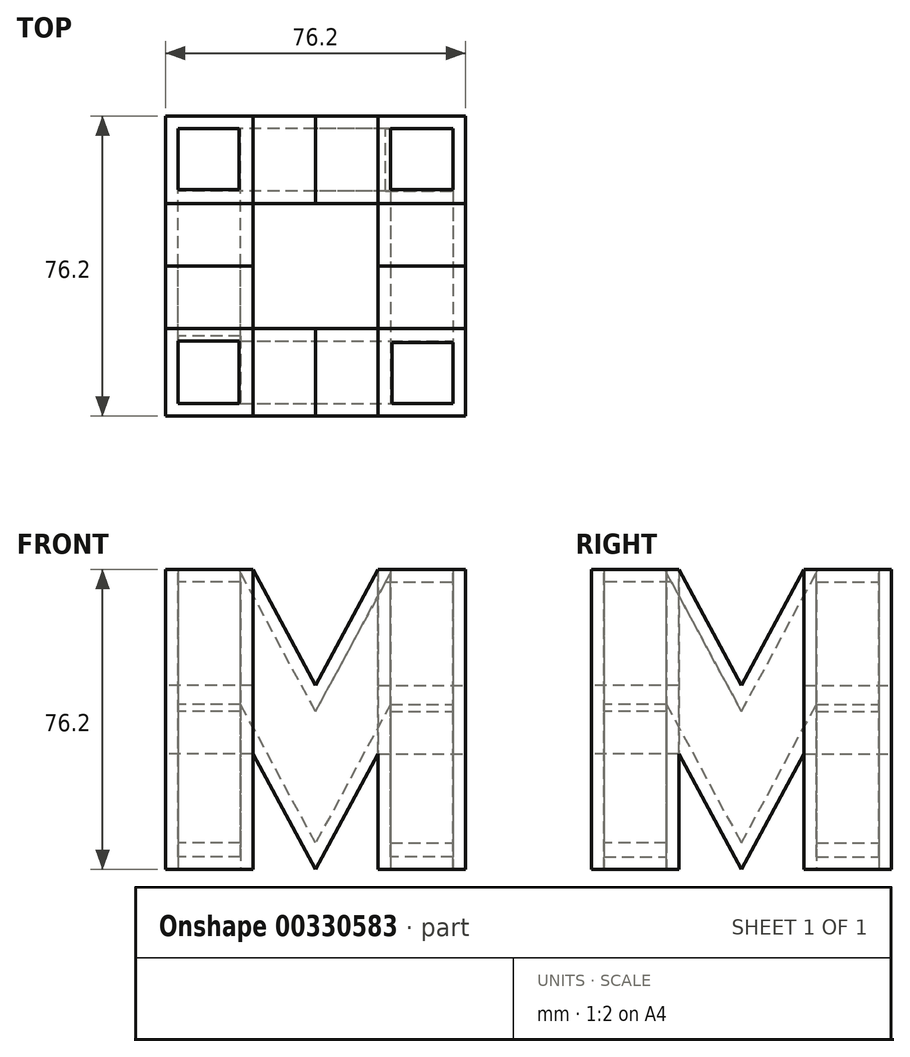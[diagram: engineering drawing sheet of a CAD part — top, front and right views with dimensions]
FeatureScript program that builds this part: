
annotation { "Feature Type Name" : "Feature", "Feature Type Description" : "" }
export const myFeature = defineFeature(function(context is Context, id is Id, definition is map)
    precondition{}
    {
        {
            var Q0;
            Q0=qCreatedBy(makeId("Front.planeOp"),FACE);
            var sketch = newSketch(context, id + "F0", { "sketchPlane" : qUnion([Q0])});
            skLineSegment(sketch, "E0.bottom", {"start": v(38.1, -38.1) * mm, "end": v(-38.1, -38.1) * mm, "construction": true});
            skLineSegment(sketch, "E0.top", {"start": v(38.1, 38.1) * mm, "end": v(-38.1, 38.1) * mm, "construction": true});
            skLineSegment(sketch, "E0.left", {"start": v(38.1, -38.1) * mm, "end": v(38.1, 38.1) * mm, "construction": true});
            skLineSegment(sketch, "E0.right", {"start": v(-38.1, -38.1) * mm, "end": v(-38.1, 38.1) * mm, "construction": true});
            skPoint(sketch, "E0.middle", {"position": v(0, 0) * mm});
            skLineSegment(sketch, "E1", {"start": v(-38.1, 38.1) * mm, "end": v(-38.1, -38.1) * mm});
            skLineSegment(sketch, "E2", {"start": v(-15.87, -38.1) * mm, "end": v(-15.87, -8.69) * mm});
            skLineSegment(sketch, "E3", {"start": v(15.88, -38.1) * mm, "end": v(38.1, -38.1) * mm});
            skLineSegment(sketch, "E4", {"start": v(38.1, 38.1) * mm, "end": v(15.88, 38.1) * mm});
            skLineSegment(sketch, "E5", {"start": v(-15.88, 38.1) * mm, "end": v(-38.1, 38.1) * mm});
            skLineSegment(sketch, "E6", {"start": v(38.1, 38.1) * mm, "end": v(38.1, -38.1) * mm});
            skLineSegment(sketch, "E7", {"start": v(-38.1, -38.1) * mm, "end": v(-15.87, -38.1) * mm});
            skLineSegment(sketch, "E8", {"start": v(-15.87, -8.69) * mm, "end": v(0, -38.1) * mm});
            skLineSegment(sketch, "E9", {"start": v(0, -38.1) * mm, "end": v(15.88, -8.69) * mm});
            skLineSegment(sketch, "E10", {"start": v(15.88, -8.69) * mm, "end": v(15.88, -38.1) * mm});
            skLineSegment(sketch, "E11", {"start": v(-15.88, 38.1) * mm, "end": v(0, 8.69) * mm});
            skLineSegment(sketch, "E12", {"start": v(0, 8.69) * mm, "end": v(15.88, 38.1) * mm});
            skLineSegment(sketch, "E13", {"start": v(15.87, -8.69) * mm, "end": v(-3.68, 1.87) * mm, "construction": true});
            skSolve(sketch);
        }
        {
            var Q0;
            Q0=makeQuery(id+"F0.imprint","IMPRINT",FACE,{"disambiguationData":[TD([[makeQuery(id+"F0.imprint","IMPRINT",EDGE,{"derivedFrom":sQuery(id+"F0.wireOp",EDGE,"E1")}),1.0]])]});
            extrude(context, id + "F1", {"entities" : qUnion([Q0]), "oppositeDirection" : true, "depth" : 22.22 * mm});
        }
        {
            var Q0;
            Q0=qCreatedBy(makeId("Top.planeOp"),FACE);
            var sketch = newSketch(context, id + "F2", { "sketchPlane" : qUnion([Q0])});
            skCircle(sketch, "E14", {"center": v(0, 38.1) * mm, "radius": 38.1 * mm, "construction": true});
            skLineSegment(sketch, "E15", {"start": v(38.1, 0) * mm, "end": v(0, 38.1) * mm, "construction": true});
            skSolve(sketch);
        }
        {
            var Q0;
            Q0=sQuery(id+"F2.wireOp",EDGE,"E15");
            var Q1;
            Q1=qCreatedBy(makeId("Right.planeOp"),FACE);
            cPlane(context, id + "F3", {"entities" : qUnion([Q0, Q1]), "cplaneType" : CPlaneType.LINE_ANGLE, "offset" : 25.4 * mm, "angle" : 0 * degree, "width" : 152.4 * mm, "height" : 152.4 * mm});
        }
        {
            var Q0;
            Q0=makeQuery(id+"F1.opExtrude","SWEPT_BODY",BODY,{"disambiguationData":[OSD([sQuery(id+"F0.wireOp",EDGE,"E1"),sQuery(id+"F0.wireOp",EDGE,"E2"),sQuery(id+"F0.wireOp",EDGE,"gpsWLYjY-ZhOC-hQn8-cpfg-05pR4dx5fST9"),sQuery(id+"F0.wireOp",EDGE,"E3"),sQuery(id+"F0.wireOp",EDGE,"E4"),sQuery(id+"F0.wireOp",EDGE,"3NluBPyZ-bMX5-kmNi-dZTR-4R4HgDXdf54k"),sQuery(id+"F0.wireOp",EDGE,"qLRwCIMz-NJTs-OjkW-UFXz-Yq7v9sXrhpcL"),sQuery(id+"F0.wireOp",EDGE,"E5"),sQuery(id+"F0.wireOp",EDGE,"E6"),sQuery(id+"F0.wireOp",EDGE,"E7")])]});
            var Q1;
            Q1=qCreatedBy(id+"F3.planeOp",FACE);
            mirror(context, id + "F4", {"operationType" : NewBodyOperationType.ADD, "entities" : qUnion([Q0]), "mirrorPlane" : qUnion([Q1])});
        }
        {
            var Q0;
            Q0=makeQuery(id+"F1.opExtrude","SWEPT_BODY",BODY,{"disambiguationData":[OSD([sQuery(id+"F0.wireOp",EDGE,"E1"),sQuery(id+"F0.wireOp",EDGE,"E2"),sQuery(id+"F0.wireOp",EDGE,"gpsWLYjY-ZhOC-hQn8-cpfg-05pR4dx5fST9"),sQuery(id+"F0.wireOp",EDGE,"E3"),sQuery(id+"F0.wireOp",EDGE,"E4"),sQuery(id+"F0.wireOp",EDGE,"3NluBPyZ-bMX5-kmNi-dZTR-4R4HgDXdf54k"),sQuery(id+"F0.wireOp",EDGE,"qLRwCIMz-NJTs-OjkW-UFXz-Yq7v9sXrhpcL"),sQuery(id+"F0.wireOp",EDGE,"E5"),sQuery(id+"F0.wireOp",EDGE,"E6"),sQuery(id+"F0.wireOp",EDGE,"E7")])]});
            var Q1;
            Q1=sQuery(id+"F2.wireOp",EDGE,"E14");
            circularPattern(context, id + "F5", {"entities" : qUnion([Q0]), "axis" : qUnion([Q1]), "angle" : 360 * degree, "instanceCount" : 2, "equalSpace" : true});
        }
        {
            var Q0;
            Q0=makeQuery(id+"F1.opExtrude","SWEPT_FACE",FACE,{"disambiguationData":[OSD([sQuery(id+"F0.wireOp",EDGE,"E5")])]});
            var Q1;
            Q1=makeQuery(id+"F1.opExtrude","SWEPT_FACE",FACE,{"disambiguationData":[OSD([sQuery(id+"F0.wireOp",EDGE,"E4")])]});
            var Q2;
            Q2=makeQuery(id+"F5.opPattern","COPY",FACE,{"derivedFrom":makeQuery(id+"F1.opExtrude","SWEPT_FACE",FACE,{"disambiguationData":[OSD([sQuery(id+"F0.wireOp",EDGE,"E4")])]}),"instanceName":"1"});
            var Q3;
            Q3=makeQuery(id+"F4.opPattern","COPY",FACE,{"derivedFrom":makeQuery(id+"F1.opExtrude","SWEPT_FACE",FACE,{"disambiguationData":[OSD([sQuery(id+"F0.wireOp",EDGE,"E5")])]}),"instanceName":"1"});
            var Q4;
            Q4=makeQuery(id+"F1.opExtrude","SWEPT_FACE",FACE,{"disambiguationData":[OSD([sQuery(id+"F0.wireOp",EDGE,"E7")])]});
            var Q5;
            Q5=makeQuery(id+"F5.opPattern","COPY",FACE,{"derivedFrom":makeQuery(id+"F1.opExtrude","SWEPT_FACE",FACE,{"disambiguationData":[OSD([sQuery(id+"F0.wireOp",EDGE,"E3")])]}),"instanceName":"1"});
            var Q6;
            Q6=makeQuery(id+"F4.opPattern","COPY",FACE,{"derivedFrom":makeQuery(id+"F1.opExtrude","SWEPT_FACE",FACE,{"disambiguationData":[OSD([sQuery(id+"F0.wireOp",EDGE,"E7")])]}),"instanceName":"1"});
            var Q7;
            Q7=makeQuery(id+"F1.opExtrude","SWEPT_FACE",FACE,{"disambiguationData":[OSD([sQuery(id+"F0.wireOp",EDGE,"E3")])]});
            shell(context, id + "F6", {"entities" : qUnion([Q0, Q1, Q2, Q3, Q4, Q5, Q6, Q7]), "thickness" : 3.17 * mm});
        }
    });
